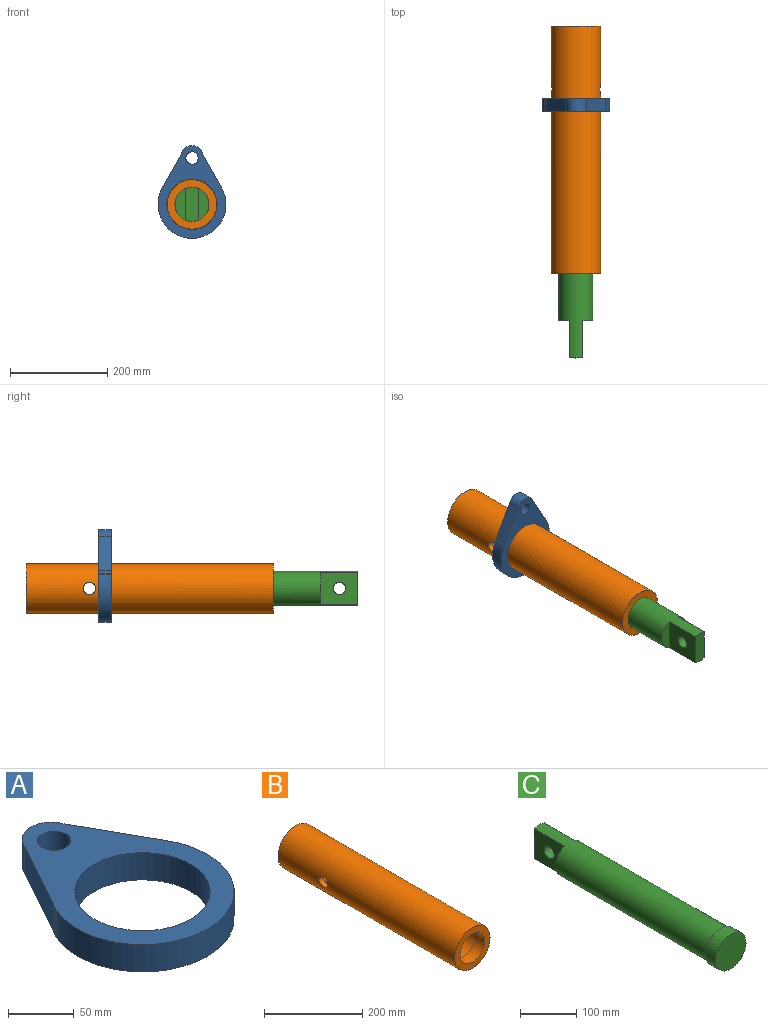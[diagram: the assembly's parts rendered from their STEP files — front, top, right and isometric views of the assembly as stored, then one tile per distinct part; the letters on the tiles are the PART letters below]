
ASSEMBLY  parts=3 mates=2
PART A: 10 faces, bbox 139.7x190.5x25.4 mm
  f0: cylinder r=69.85mm len=139.7mm, axis (0,0,-1), area 7228.5mm2, adj f1,f6,f8,f9
  f1: plane 71.52x39.94mm, normal (0.87,0.49,0), area 2080.8mm2, adj f0,f2,f8,f9
  f2: cylinder r=22.23mm len=42.09mm, axis (0,0,-1), area 1403.8mm2, adj f1,f3,f8,f9
  f3: plane 69.5x38.77mm, normal (-0.87,0.49,0), area 2021.4mm2, adj f2,f4,f8,f9
  f4: plane 25.4x5.88mm, normal (-0.86,0.52,0), area 174.3mm2, adj f3,f6,f8,f9
  f5: cylinder r=12.7mm len=25.4mm, axis (0,0,-1), area 2026.8mm2, adj f8,f9
  f6: plane 25.4x1.49mm, normal (-0.98,0.21,0), area 38.7mm2, adj f0,f4,f8,f9
  f7: cylinder r=51.56mm len=103.12mm, axis (0,0,-1), area 8228.9mm2, adj f8,f9
  f8: plane 190.5x139.7mm, normal (0,0,1), area 9696.3mm2, adj f0,f1,f2,f3,f4,f5,f6,f7
  f9: plane 190.5x139.7mm, normal (0,0,-1), area 9696.3mm2, adj f0,f1,f2,f3,f4,f5,f6,f7
PART B: 8 faces, bbox 101.6x508x101.6 mm
  f0: cylinder r=50.8mm len=508mm, axis (0,-1,0), area 161126.4mm2, adj f2,f5,f6,f7
  f1: cylinder r=38.1mm len=482.6mm, axis (0,-1,0), area 114505mm2, adj f4,f5,f6,f7
  f2: plane 101.6x101.6mm, normal (0,-1,0), area 4275.3mm2, adj f0,f3
  f3: cylinder r=34.92mm len=69.85mm, axis (0,-1,0), area 5573.8mm2, adj f2,f4
  f4: plane 76.2x76.2mm, normal (0,1,0), area 728.4mm2, adj f1,f3
  f5: plane 101.6x101.6mm, normal (0,1,0), area 3547mm2, adj f0,f1
  f6: cylinder r=12.7mm len=25.4mm, axis (1,0,0), area 1035.6mm2, adj f0,f1
  f7: cylinder r=12.7mm len=25.4mm, axis (-1,0,0), area 1035.6mm2, adj f0,f1
PART C: 10 faces, bbox 76.2x482.6x76.2 mm
  f0: plane 69.85x25.4mm, normal (0,1,0), area 1734.3mm2, adj f2,f5,f7
  f1: plane 76.2x76.2mm, normal (0,-1,0), area 4560.4mm2, adj f4
  f2: cylinder r=34.92mm len=457.2mm, axis (0,1,0), area 87568.5mm2, adj f0,f3,f5,f6,f7,f8
  f3: plane 76.2x76.2mm, normal (0,1,0), area 728.4mm2, adj f2,f4
  f4: cylinder r=38.1mm len=76.2mm, axis (0,1,0), area 6080.5mm2, adj f1,f3
  f5: plane 76.2x65.07mm, normal (1,0,0), area 4451.5mm2, adj f0,f2,f6,f9
  f6: plane 65.07x22.23mm, normal (0,1,0), area 1048.9mm2, adj f2,f5
  f7: plane 76.2x65.07mm, normal (-1,0,0), area 4451.5mm2, adj f0,f2,f8,f9
  f8: plane 65.07x22.23mm, normal (0,1,0), area 1048.9mm2, adj f2,f7
  f9: cylinder r=12.7mm len=25.4mm, axis (1,0,0), area 2026.8mm2, adj f5,f7
PLACE A rot(axis=(1,0,0),90deg) t=(-388.79,-602.79,204.39)mm
PLACE B rot(axis=(-0.01,-0.05,-1),0deg) t=(-388.79,-743.91,204.39)mm
PLACE C rot(axis=(0,0,1),180deg) t=(-388.79,-1005.43,204.39)mm
MATE slider A.f7 <-> B.f0  axis (0,-1,0) through (-388.79,-628.19,204.39)mm
MATE slider C.f2 <-> B.f0  axis (0,1,0) through (-388.79,-652.62,204.39)mm
